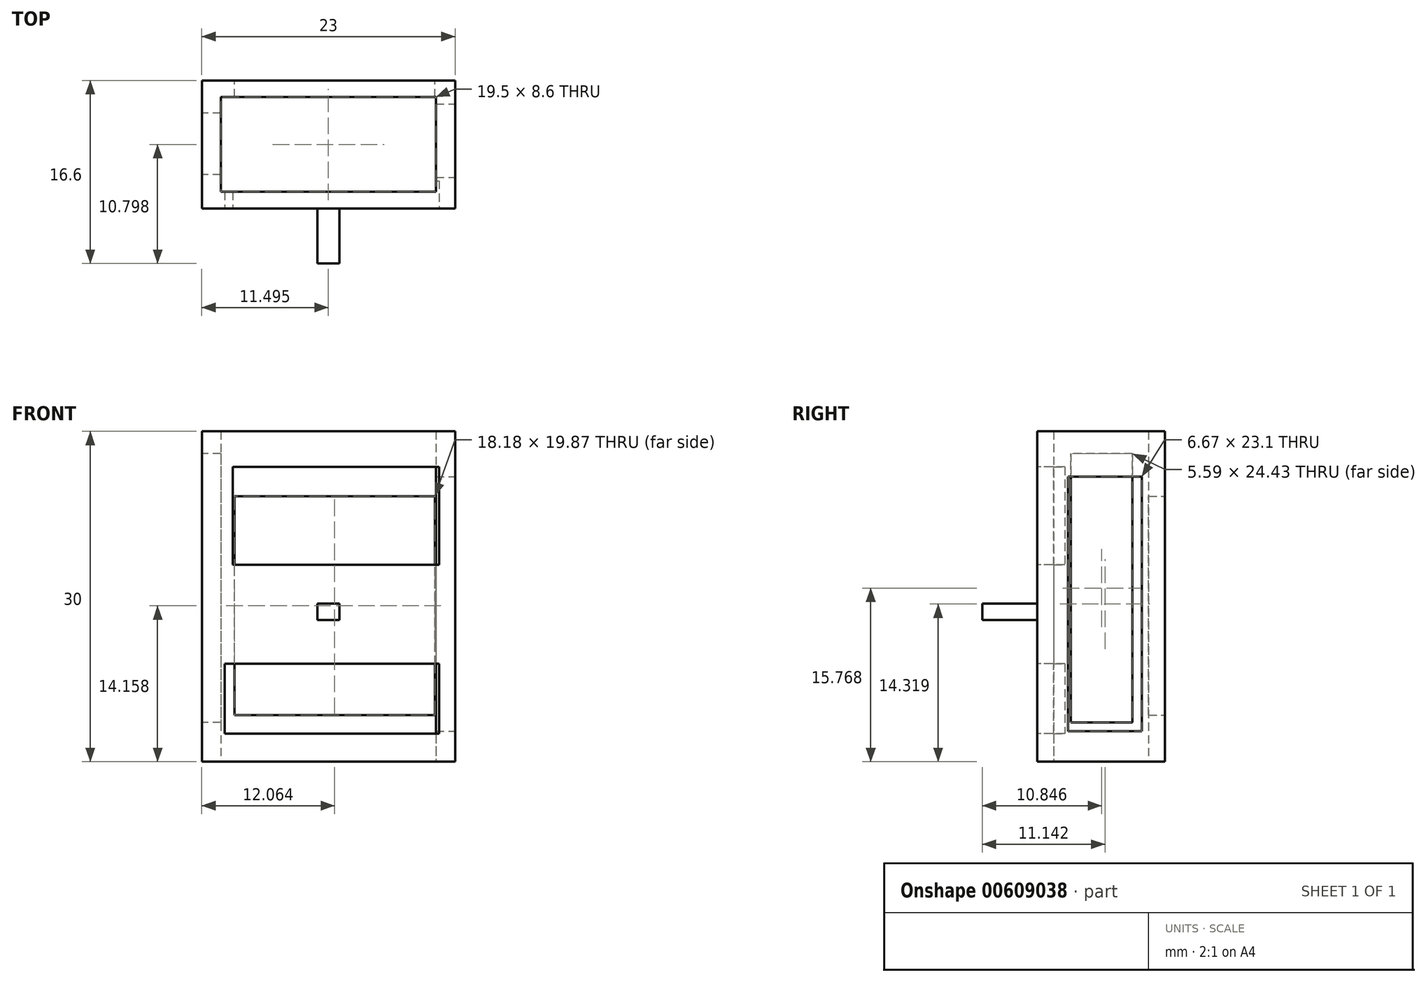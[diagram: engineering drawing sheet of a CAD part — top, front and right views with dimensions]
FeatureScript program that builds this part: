
annotation { "Feature Type Name" : "Feature", "Feature Type Description" : "" }
export const myFeature = defineFeature(function(context is Context, id is Id, definition is map)
    precondition{}
    {
        {
            var Q0;
            Q0=qCreatedBy(makeId("Top.planeOp"),FACE);
            var sketch = newSketch(context, id + "F0", { "sketchPlane" : qUnion([Q0])});
            skLineSegment(sketch, "E0.bottom", {"start": v(-14.58, 36.84) * mm, "end": v(4.92, 36.84) * mm});
            skLineSegment(sketch, "E0.top", {"start": v(-14.58, 28.24) * mm, "end": v(4.92, 28.24) * mm});
            skLineSegment(sketch, "E0.left", {"start": v(-14.58, 36.84) * mm, "end": v(-14.58, 28.24) * mm});
            skLineSegment(sketch, "E0.right", {"start": v(4.92, 36.84) * mm, "end": v(4.92, 28.24) * mm});
            skLineSegment(sketch, "E1.bottom", {"start": v(-16.32, 38.34) * mm, "end": v(6.68, 38.34) * mm});
            skLineSegment(sketch, "E1.top", {"start": v(-16.32, 26.74) * mm, "end": v(6.68, 26.74) * mm});
            skLineSegment(sketch, "E1.left", {"start": v(-16.32, 38.34) * mm, "end": v(-16.32, 26.74) * mm});
            skLineSegment(sketch, "E1.right", {"start": v(6.68, 38.34) * mm, "end": v(6.68, 26.74) * mm});
            skLineSegment(sketch, "E2.bottom", {"start": v(-3.3, 28.24) * mm, "end": v(-3.16, 28.24) * mm});
            skLineSegment(sketch, "E2.top", {"start": v(-3.3, 26.74) * mm, "end": v(-3.16, 26.74) * mm});
            skLineSegment(sketch, "E3.bottom", {"start": v(-5.62, 38.34) * mm, "end": v(-5.5, 38.34) * mm});
            skLineSegment(sketch, "E3.top", {"start": v(-5.63, 36.84) * mm, "end": v(-5.5, 36.84) * mm});
            skLineSegment(sketch, "E4.left", {"start": v(-16.32, 32.54) * mm, "end": v(-16.32, 32.54) * mm});
            skLineSegment(sketch, "E4.right", {"start": v(-14.58, 32.54) * mm, "end": v(-14.58, 32.1) * mm});
            skSolve(sketch);
        }
        {
            var Q0;
            {var subQ7=sQuery(id+"F0.wireOp",EDGE,"E0.left");Q0=makeQuery(id+"F0.imprint","IMPRINT",FACE,{"disambiguationData":[TD([[makeQuery(id+"F0.imprint","IMPRINT",EDGE,{"derivedFrom":subQ7}),-1.0]])]});}
            extrude(context, id + "F1", {"entities" : qUnion([Q0]), "depth" : 30 * mm, "offsetDistance" : 25 * mm});
        }
        {
            var Q0;
            Q0=makeQuery(id+"F1.opExtrude","SWEPT_FACE",FACE,{"disambiguationData":[OSD([sQuery(id+"F0.wireOp",EDGE,"E1.right")])]});
            var sketch = newSketch(context, id + "F2", { "sketchPlane" : qUnion([Q0])});
            skLineSegment(sketch, "E5.bottom", {"start": v(36.22, 25.87) * mm, "end": v(29.55, 25.87) * mm});
            skLineSegment(sketch, "E5.top", {"start": v(36.22, 2.77) * mm, "end": v(29.55, 2.77) * mm});
            skLineSegment(sketch, "E5.left", {"start": v(36.22, 25.87) * mm, "end": v(36.22, 2.77) * mm});
            skLineSegment(sketch, "E5.right", {"start": v(29.55, 25.87) * mm, "end": v(29.55, 2.77) * mm});
            skSolve(sketch);
        }
        {
            var Q0;
            Q0=makeQuery(id+"F2.imprint","IMPRINT",FACE,{"disambiguationData":[TD([[makeQuery(id+"F2.imprint","IMPRINT",EDGE,{"derivedFrom":sQuery(id+"F2.wireOp",EDGE,"E5.bottom")}),1.0]])]});
            extrude(context, id + "F3", {"entities" : qUnion([Q0]), "operationType" : NewBodyOperationType.REMOVE, "oppositeDirection" : true, "depth" : 2.5 * mm, "offsetDistance" : 25 * mm});
        }
        {
            var Q0;
            Q0=makeQuery(id+"F1.opExtrude","SWEPT_FACE",FACE,{"disambiguationData":[OSD([sQuery(id+"F0.wireOp",EDGE,"E1.left")])]});
            var sketch = newSketch(context, id + "F4", { "sketchPlane" : qUnion([Q0])});
            skLineSegment(sketch, "E6.bottom", {"start": v(-35.38, 3.55) * mm, "end": v(-29.8, 3.55) * mm});
            skLineSegment(sketch, "E6.top", {"start": v(-35.38, 27.98) * mm, "end": v(-29.8, 27.98) * mm});
            skLineSegment(sketch, "E6.left", {"start": v(-35.38, 3.55) * mm, "end": v(-35.38, 27.98) * mm});
            skLineSegment(sketch, "E6.right", {"start": v(-29.8, 3.55) * mm, "end": v(-29.8, 27.98) * mm});
            skSolve(sketch);
        }
        {
            var Q0;
            Q0=makeQuery(id+"F4.imprint","IMPRINT",FACE,{"disambiguationData":[TD([[makeQuery(id+"F4.imprint","IMPRINT",EDGE,{"derivedFrom":sQuery(id+"F4.wireOp",EDGE,"E6.bottom")}),1.0]])]});
            extrude(context, id + "F5", {"entities" : qUnion([Q0]), "operationType" : NewBodyOperationType.REMOVE, "oppositeDirection" : true, "depth" : 2.5 * mm, "offsetDistance" : 25 * mm});
        }
        {
            var Q0;
            Q0=makeQuery(id+"F1.opExtrude","SWEPT_FACE",FACE,{"disambiguationData":[OSD([sQuery(id+"F0.wireOp",EDGE,"E1.bottom"),sQuery(id+"F0.wireOp",EDGE,"E3.bottom")])]});
            var sketch = newSketch(context, id + "F6", { "sketchPlane" : qUnion([Q0])});
            skLineSegment(sketch, "E7.bottom", {"start": v(13.35, 4.22) * mm, "end": v(-4.84, 4.22) * mm});
            skLineSegment(sketch, "E7.top", {"start": v(13.35, 24.1) * mm, "end": v(-4.84, 24.1) * mm});
            skLineSegment(sketch, "E7.left", {"start": v(13.35, 4.22) * mm, "end": v(13.35, 24.1) * mm});
            skLineSegment(sketch, "E7.right", {"start": v(-4.84, 4.22) * mm, "end": v(-4.84, 24.1) * mm});
            skSolve(sketch);
        }
        {
            var Q0;
            Q0 = qSketchRegion(id + "F6", true);
            extrude(context, id + "F7", {"entities" : qUnion([Q0]), "operationType" : NewBodyOperationType.REMOVE, "oppositeDirection" : true, "depth" : 2.5 * mm, "offsetDistance" : 25 * mm});
        }
        {
            var Q0;
            Q0=makeQuery(id+"F1.opExtrude","SWEPT_FACE",FACE,{"disambiguationData":[OSD([sQuery(id+"F0.wireOp",EDGE,"E1.top"),sQuery(id+"F0.wireOp",EDGE,"E2.top")])]});
            var sketch = newSketch(context, id + "F8", { "sketchPlane" : qUnion([Q0])});
            skLineSegment(sketch, "E8.bottom", {"start": v(-16.32, 16.5) * mm, "end": v(6.68, 16.5) * mm});
            skLineSegment(sketch, "E8.top", {"start": v(-16.32, 11.73) * mm, "end": v(6.68, 11.73) * mm});
            skLineSegment(sketch, "E8.left", {"start": v(-16.32, 16.5) * mm, "end": v(-16.32, 11.73) * mm});
            skLineSegment(sketch, "E8.right", {"start": v(6.68, 16.5) * mm, "end": v(6.68, 11.73) * mm});
            skLineSegment(sketch, "E9.bottom", {"start": v(-13.5, 26.77) * mm, "end": v(5.21, 26.77) * mm});
            skLineSegment(sketch, "E9.top", {"start": v(-13.5, 17.87) * mm, "end": v(5.21, 17.87) * mm});
            skLineSegment(sketch, "E9.left", {"start": v(-13.5, 26.77) * mm, "end": v(-13.5, 17.87) * mm});
            skLineSegment(sketch, "E9.right", {"start": v(5.21, 26.77) * mm, "end": v(5.21, 17.87) * mm});
            skLineSegment(sketch, "E10.bottom", {"start": v(-14.23, 8.89) * mm, "end": v(5.21, 8.89) * mm});
            skLineSegment(sketch, "E10.top", {"start": v(-14.23, 2.56) * mm, "end": v(5.21, 2.56) * mm});
            skLineSegment(sketch, "E10.left", {"start": v(-14.23, 8.89) * mm, "end": v(-14.23, 2.56) * mm});
            skLineSegment(sketch, "E10.right", {"start": v(5.21, 8.89) * mm, "end": v(5.21, 2.56) * mm});
            skSolve(sketch);
        }
        {
            var Q0;
            Q0=makeQuery(id+"F8.imprint","IMPRINT",FACE,{"disambiguationData":[TD([[makeQuery(id+"F8.imprint","IMPRINT",EDGE,{"derivedFrom":sQuery(id+"F8.wireOp",EDGE,"E10.bottom")}),-1.0]])]});
            var Q1;
            Q1=makeQuery(id+"F8.imprint","IMPRINT",FACE,{"disambiguationData":[TD([[makeQuery(id+"F8.imprint","IMPRINT",EDGE,{"derivedFrom":sQuery(id+"F8.wireOp",EDGE,"E9.bottom")}),-1.0]])]});
            extrude(context, id + "F9", {"entities" : qUnion([Q0, Q1]), "operationType" : NewBodyOperationType.REMOVE, "oppositeDirection" : true, "depth" : 2.5 * mm, "offsetDistance" : 25 * mm});
        }
        {
            var Q0;
            Q0=makeQuery(id+"F1.opExtrude","SWEPT_FACE",FACE,{"disambiguationData":[OSD([sQuery(id+"F0.wireOp",EDGE,"E1.top"),sQuery(id+"F0.wireOp",EDGE,"E2.top")])]});
            var sketch = newSketch(context, id + "F10", { "sketchPlane" : qUnion([Q0])});
            skLineSegment(sketch, "E11.bottom", {"start": v(-5.82, 14.35) * mm, "end": v(-3.82, 14.35) * mm});
            skLineSegment(sketch, "E11.top", {"start": v(-5.82, 12.85) * mm, "end": v(-3.82, 12.85) * mm});
            skLineSegment(sketch, "E11.left", {"start": v(-5.82, 14.35) * mm, "end": v(-5.82, 12.85) * mm});
            skLineSegment(sketch, "E11.right", {"start": v(-3.82, 14.35) * mm, "end": v(-3.82, 12.85) * mm});
            skSolve(sketch);
        }
        {
            var Q0;
            Q0=makeQuery(id+"F10.imprint","IMPRINT",FACE,{"disambiguationData":[TD([[makeQuery(id+"F10.imprint","IMPRINT",EDGE,{"derivedFrom":sQuery(id+"F10.wireOp",EDGE,"E11.bottom")}),-1.0]])]});
            extrude(context, id + "F11", {"entities" : qUnion([Q0]), "operationType" : NewBodyOperationType.ADD, "depth" : 5 * mm, "offsetDistance" : 25 * mm});
        }
    });
